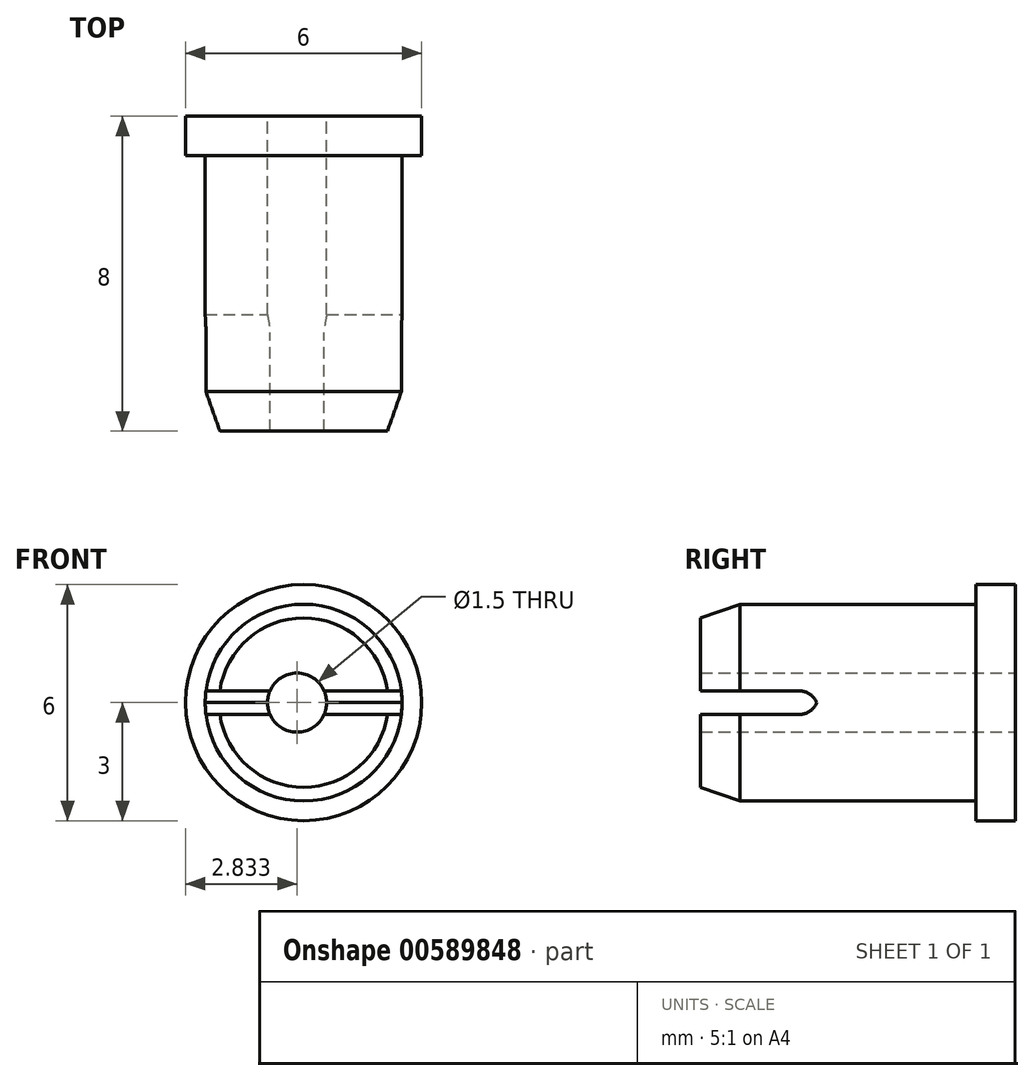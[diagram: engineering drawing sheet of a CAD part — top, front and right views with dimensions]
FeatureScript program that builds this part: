
annotation { "Feature Type Name" : "Feature", "Feature Type Description" : "" }
export const myFeature = defineFeature(function(context is Context, id is Id, definition is map)
    precondition{}
    {
        {
            var Q0;
            Q0=qCreatedBy(makeId("Front.planeOp"),FACE);
            var sketch = newSketch(context, id + "F0", { "sketchPlane" : qUnion([Q0])});
            skCircle(sketch, "E0", {"center": v(0, 0) * mm, "radius": 2.5 * mm});
            skSolve(sketch);
        }
        {
            var Q0;
            Q0 = qSketchRegion(id + "F0", true);
            extrude(context, id + "F1", {"entities" : qUnion([Q0]), "depth" : 6 * mm, "offsetDistance" : 25 * mm});
        }
        {
            var Q0;
            Q0=makeQuery(id+"F1.opExtrude","CAP_FACE",FACE,{"disambiguationData":[OSD([sQuery(id+"F0.wireOp",EDGE,"E0")])],"isStart":false});
            cPlane(context, id + "F2", {"entities" : qUnion([Q0]), "cplaneType" : CPlaneType.OFFSET, "offset" : 1 * mm, "width" : 150 * mm, "height" : 150 * mm});
        }
        {
            var Q0;
            Q0=qCreatedBy(id+"F2.planeOp",FACE);
            var sketch = newSketch(context, id + "F3", { "sketchPlane" : qUnion([Q0])});
            skCircle(sketch, "E1", {"center": v(0, 0) * mm, "radius": 2.15 * mm});
            skSolve(sketch);
        }
        {
            var Q1;
            Q1=makeQuery(id+"F3.imprint","IMPRINT",FACE,{"disambiguationData":[TD([[makeQuery(id+"F3.imprint","IMPRINT",EDGE,{"derivedFrom":sQuery(id+"F3.wireOp",EDGE,"E1")}),1.0]])]});
            var Q2;
            Q2=makeQuery(id+"F1.opExtrude","CAP_FACE",FACE,{"disambiguationData":[OSD([sQuery(id+"F0.wireOp",EDGE,"E0")])],"isStart":false});
            loft(context, id + "F4", {"operationType" : NewBodyOperationType.ADD, "sheetProfilesArray" : [{ "sheetProfileEntities" : qUnion([Q1]) }, { "sheetProfileEntities" : qUnion([Q2]) }]});
        }
        {
            var Q0;
            Q0=makeQuery(id+"F1.opExtrude","CAP_FACE",FACE,{"disambiguationData":[OSD([sQuery(id+"F0.wireOp",EDGE,"E0")])],"isStart":true});
            cPlane(context, id + "F5", {"entities" : qUnion([Q0]), "cplaneType" : CPlaneType.OFFSET, "offset" : 0 * mm, "width" : 150 * mm, "height" : 150 * mm});
        }
        {
            var Q0;
            Q0=qCreatedBy(id+"F5.planeOp",FACE);
            var sketch = newSketch(context, id + "F6", { "sketchPlane" : qUnion([Q0])});
            skCircle(sketch, "E2", {"center": v(0, 0) * mm, "radius": 3 * mm});
            skSolve(sketch);
        }
        {
            var Q0;
            Q0 = qSketchRegion(id + "F6", true);
            extrude(context, id + "F7", {"entities" : qUnion([Q0]), "operationType" : NewBodyOperationType.ADD, "depth" : 1 * mm, "offsetDistance" : 25 * mm});
        }
        {
            var Q0;
            Q0=makeQuery(id+"F7.opExtrude","CAP_FACE",FACE,{"disambiguationData":[OSD([sQuery(id+"F6.wireOp",EDGE,"E2")])],"isStart":false});
            cPlane(context, id + "F8", {"entities" : qUnion([Q0]), "cplaneType" : CPlaneType.OFFSET, "offset" : 0 * mm, "width" : 150 * mm, "height" : 150 * mm});
        }
        {
            var Q0;
            Q0=qCreatedBy(id+"F8.planeOp",FACE);
            var sketch = newSketch(context, id + "F9", { "sketchPlane" : qUnion([Q0])});
            skCircle(sketch, "E3", {"center": v(0.17, 0) * mm, "radius": 0.75 * mm});
            skSolve(sketch);
        }
        {
            var Q0;
            Q0 = qSketchRegion(id + "F9", true);
            extrude(context, id + "F10", {"entities" : qUnion([Q0]), "operationType" : NewBodyOperationType.REMOVE, "endBound" : BoundingType.THROUGH_ALL, "oppositeDirection" : true, "depth" : 25 * mm, "offsetDistance" : 25 * mm});
        }
        {
            var Q0;
            Q0=makeQuery(id+"F4.opLoft","CAP_FACE",FACE,{"disambiguationData":[OSD([makeQuery(id+"F3.imprint","IMPRINT",FACE,{"disambiguationData":[TD([[makeQuery(id+"F3.imprint","IMPRINT",EDGE,{"derivedFrom":sQuery(id+"F3.wireOp",EDGE,"E1")}),1.0]])]})])],"isStart":true});
            cPlane(context, id + "F11", {"entities" : qUnion([Q0]), "cplaneType" : CPlaneType.OFFSET, "offset" : 0 * mm, "width" : 150 * mm, "height" : 150 * mm});
        }
        {
            var Q0;
            Q0=qCreatedBy(id+"F11.planeOp",FACE);
            var sketch = newSketch(context, id + "F12", { "sketchPlane" : qUnion([Q0])});
            skLineSegment(sketch, "E4", {"start": v(-1.88, 0) * mm, "end": v(2.6, 0) * mm, "construction": true});
            skLineSegment(sketch, "E5", {"start": v(0, -3.37) * mm, "end": v(0, 2.03) * mm, "construction": true});
            skLineSegment(sketch, "E6.bottom", {"start": v(0, 0) * mm, "end": v(3, 0) * mm});
            skLineSegment(sketch, "E6.top", {"start": v(0, 0.3) * mm, "end": v(3, 0.3) * mm});
            skLineSegment(sketch, "E6.left", {"start": v(0, 0) * mm, "end": v(0, 0.3) * mm});
            skLineSegment(sketch, "E6.right", {"start": v(3, 0) * mm, "end": v(3, 0.3) * mm});
            skLineSegment(sketch, "E7.MirrorCS", {"start": v(0, 0.3) * mm, "end": v(-3, 0.3) * mm});
            skLineSegment(sketch, "E8.MirrorCS", {"start": v(-3, 0) * mm, "end": v(-3, 0.3) * mm});
            skLineSegment(sketch, "E9.MirrorCS", {"start": v(-3, 0) * mm, "end": v(-3, -0.3) * mm});
            skLineSegment(sketch, "E10.MirrorCS", {"start": v(0, -0.3) * mm, "end": v(-3, -0.3) * mm});
            skLineSegment(sketch, "E11.MirrorCS", {"start": v(0, -0.3) * mm, "end": v(3, -0.3) * mm});
            skLineSegment(sketch, "E12.MirrorCS", {"start": v(3, 0) * mm, "end": v(3, -0.3) * mm});
            skSolve(sketch);
        }
        {
            var Q0;
            Q0 = qSketchRegion(id + "F12", true);
            extrude(context, id + "F13", {"entities" : qUnion([Q0]), "operationType" : NewBodyOperationType.REMOVE, "oppositeDirection" : true, "depth" : 3 * mm, "offsetDistance" : 25 * mm});
        }
        {
            var Q0;
            Q0=makeQuery(id+"F13.boolean.opBoolean","COPY",EDGE,{"disambiguationData":[OD(1.0)],"derivedFrom":makeQuery(id+"F13.opExtrude","CAP_EDGE",EDGE,{"disambiguationData":[OSD([sQuery(id+"F12.wireOp",EDGE,"E10.MirrorCS"),sQuery(id+"F12.wireOp",EDGE,"E11.MirrorCS")])],"isStart":false})});
            var Q1;
            Q1=makeQuery(id+"F13.boolean.opBoolean","COPY",EDGE,{"disambiguationData":[OD(1.0)],"derivedFrom":makeQuery(id+"F13.opExtrude","CAP_EDGE",EDGE,{"disambiguationData":[OSD([sQuery(id+"F12.wireOp",EDGE,"E6.top"),sQuery(id+"F12.wireOp",EDGE,"E7.MirrorCS")])],"isStart":false})});
            var Q2;
            Q2=makeQuery(id+"F13.boolean.opBoolean","COPY",EDGE,{"disambiguationData":[OD(0.0)],"derivedFrom":makeQuery(id+"F13.opExtrude","CAP_EDGE",EDGE,{"disambiguationData":[OSD([sQuery(id+"F12.wireOp",EDGE,"E10.MirrorCS"),sQuery(id+"F12.wireOp",EDGE,"E11.MirrorCS")])],"isStart":false})});
            var Q3;
            Q3=makeQuery(id+"F13.boolean.opBoolean","COPY",EDGE,{"disambiguationData":[OD(0.0)],"derivedFrom":makeQuery(id+"F13.opExtrude","CAP_EDGE",EDGE,{"disambiguationData":[OSD([sQuery(id+"F12.wireOp",EDGE,"E6.top"),sQuery(id+"F12.wireOp",EDGE,"E7.MirrorCS")])],"isStart":false})});
            fillet(context, id + "F14", {"entities" : qUnion([Q0, Q1, Q2, Q3]), "radius" : 0.5 * mm, "tangentPropagation" : true, "allowEdgeOverflow" : false});
        }
    });
